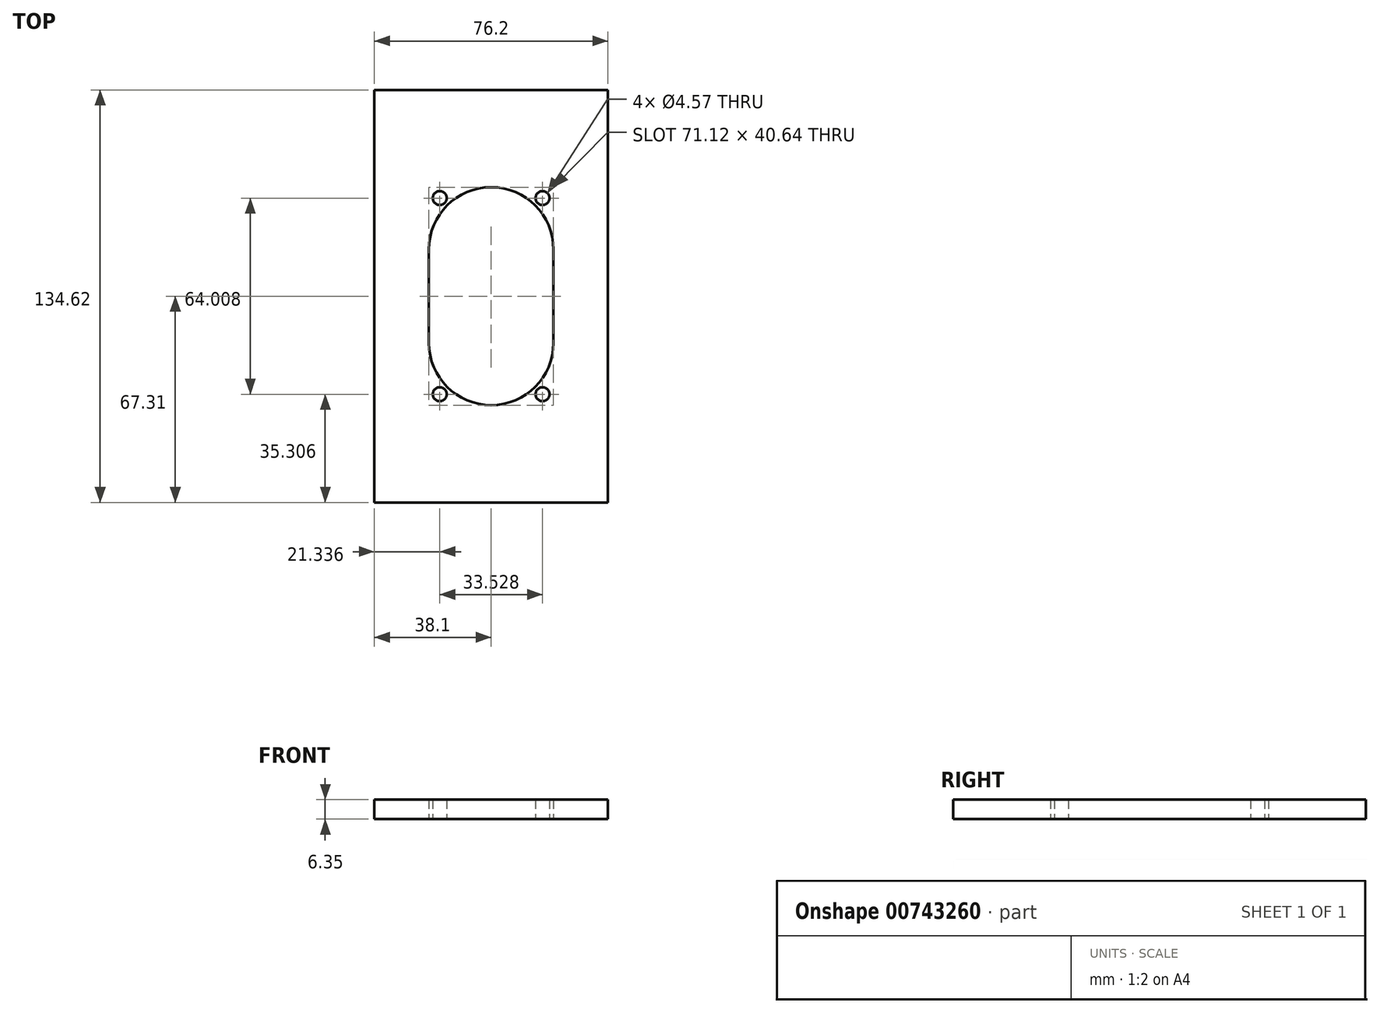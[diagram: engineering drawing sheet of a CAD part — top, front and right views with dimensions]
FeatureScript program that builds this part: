
annotation { "Feature Type Name" : "Feature", "Feature Type Description" : "" }
export const myFeature = defineFeature(function(context is Context, id is Id, definition is map)
    precondition{}
    {
        {
            var Q0;
            Q0=qCreatedBy(makeId("Top.planeOp"),FACE);
            var sketch = newSketch(context, id + "F0", { "sketchPlane" : qUnion([Q0])});
            skLineSegment(sketch, "E0.bottom", {"start": v(-38.1, 67.3) * mm, "end": v(38.1, 67.31) * mm});
            skLineSegment(sketch, "E0.top", {"start": v(-38.1, -67.31) * mm, "end": v(38.1, -67.31) * mm});
            skLineSegment(sketch, "E0.left", {"start": v(-38.1, 67.3) * mm, "end": v(-38.1, -67.31) * mm});
            skLineSegment(sketch, "E0.right", {"start": v(38.1, 67.31) * mm, "end": v(38.1, -67.31) * mm});
            skPoint(sketch, "E0.middle", {"position": v(0, 0) * mm});
            skLineSegment(sketch, "E1.bottom", {"start": v(20.32, 35.56) * mm, "end": v(-20.32, 35.56) * mm});
            skLineSegment(sketch, "E1.top", {"start": v(20.32, -35.56) * mm, "end": v(-20.32, -35.56) * mm});
            skLineSegment(sketch, "E1.left", {"start": v(20.32, 35.56) * mm, "end": v(20.32, -35.56) * mm});
            skLineSegment(sketch, "E1.right", {"start": v(-20.32, 35.56) * mm, "end": v(-20.32, -35.56) * mm});
            skPoint(sketch, "E2.first.point", {"position": v(0, -35.56) * mm});
            skCircle(sketch, "E3", {"center": v(0, -15.24) * mm, "radius": 20.32 * mm});
            skCircle(sketch, "E4", {"center": v(0, 15.24) * mm, "radius": 20.32 * mm});
            skCircle(sketch, "E5", {"center": v(-16.76, -32) * mm, "radius": 2.29 * mm});
            skCircle(sketch, "E6", {"center": v(16.76, -32) * mm, "radius": 2.29 * mm});
            skCircle(sketch, "E7", {"center": v(-16.76, 32) * mm, "radius": 2.29 * mm});
            skCircle(sketch, "E8", {"center": v(16.76, 32) * mm, "radius": 2.29 * mm});
            skSolve(sketch);
        }
        {
            var Q0;
            Q0=makeQuery(id+"F0.imprint","IMPRINT",FACE,{"disambiguationData":[TD([[makeQuery(id+"F0.imprint","IMPRINT",EDGE,{"derivedFrom":sQuery(id+"F0.wireOp",EDGE,"E0.bottom")}),-1.0]])]});
            var Q1;
            Q1=makeQuery(id+"F0.imprint","IMPRINT",FACE,{"disambiguationData":[TD([[makeQuery(id+"F0.imprint","IMPRINT",EDGE,{"derivedFrom":sQuery(id+"F0.wireOp",EDGE,"E5")}),-1.0]])]});
            var Q2;
            Q2=makeQuery(id+"F0.imprint","IMPRINT",FACE,{"disambiguationData":[TD([[makeQuery(id+"F0.imprint","IMPRINT",EDGE,{"derivedFrom":sQuery(id+"F0.wireOp",EDGE,"E6")}),-1.0]])]});
            var Q3;
            Q3=makeQuery(id+"F0.imprint","IMPRINT",FACE,{"disambiguationData":[TD([[makeQuery(id+"F0.imprint","IMPRINT",EDGE,{"derivedFrom":sQuery(id+"F0.wireOp",EDGE,"E7")}),-1.0]])]});
            var Q4;
            Q4=makeQuery(id+"F0.imprint","IMPRINT",FACE,{"disambiguationData":[TD([[makeQuery(id+"F0.imprint","IMPRINT",EDGE,{"derivedFrom":sQuery(id+"F0.wireOp",EDGE,"E8")}),-1.0]])]});
            extrude(context, id + "F1", {"entities" : qUnion([Q0, Q1, Q2, Q3, Q4]), "depth" : 6.35 * mm, "offsetDistance" : 25.4 * mm});
        }
        {
            var Q0;
            Q0=qCreatedBy(makeId("Top.planeOp"),FACE);
            cPlane(context, id + "F2", {"entities" : qUnion([Q0]), "cplaneType" : CPlaneType.OFFSET, "offset" : 2.54 * mm, "oppositeDirection" : true, "width" : 152.4 * mm, "height" : 152.4 * mm});
        }
    });
